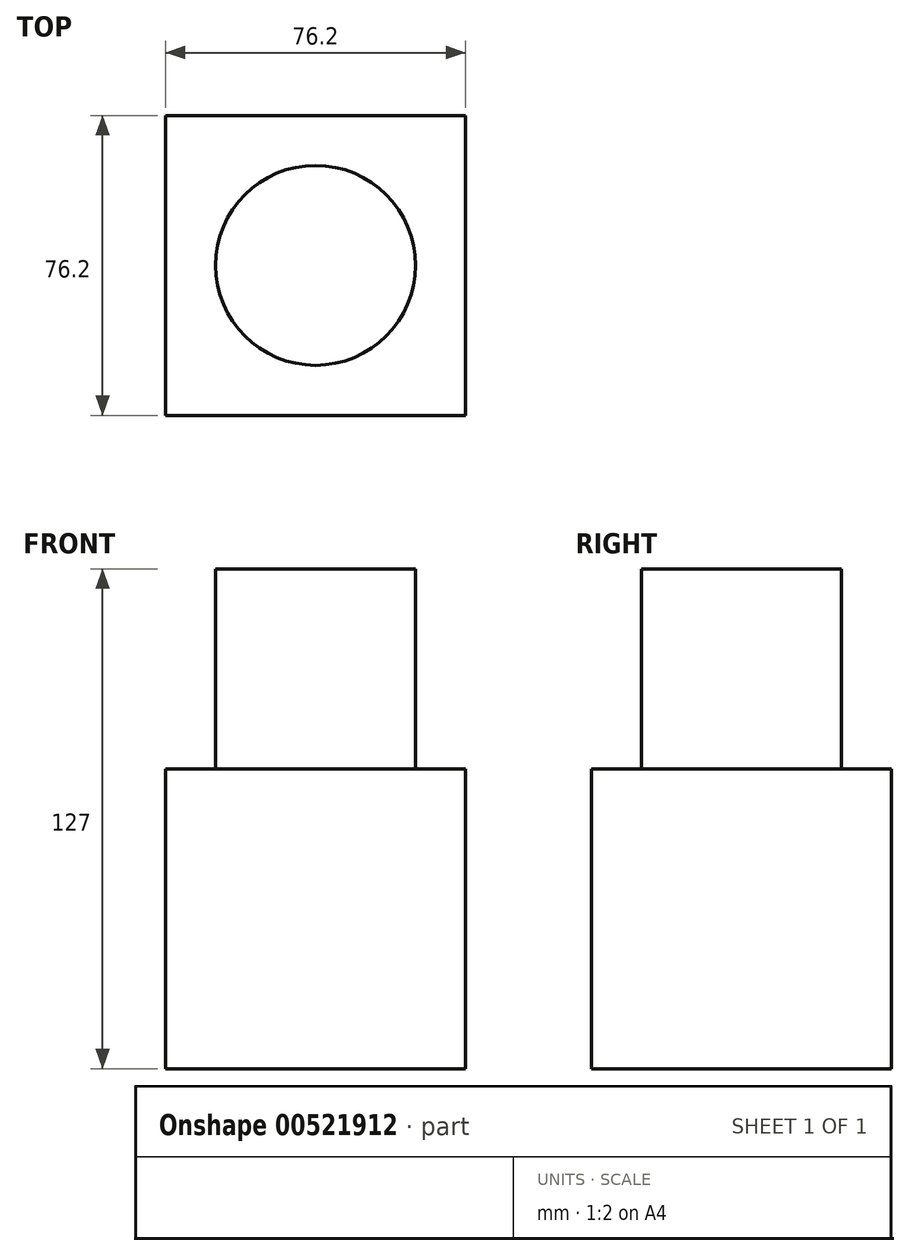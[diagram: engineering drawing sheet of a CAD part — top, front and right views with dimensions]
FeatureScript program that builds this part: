
annotation { "Feature Type Name" : "Feature", "Feature Type Description" : "" }
export const myFeature = defineFeature(function(context is Context, id is Id, definition is map)
    precondition{}
    {
        {
            var Q0;
            Q0=qCreatedBy(makeId("Top.planeOp"),FACE);
            var sketch = newSketch(context, id + "F0", { "sketchPlane" : qUnion([Q0])});
            skLineSegment(sketch, "E0.bottom", {"start": v(-38.1, -38.1) * mm, "end": v(38.1, -38.1) * mm});
            skLineSegment(sketch, "E0.top", {"start": v(-38.1, 38.1) * mm, "end": v(38.1, 38.1) * mm});
            skLineSegment(sketch, "E0.left", {"start": v(-38.1, -38.1) * mm, "end": v(-38.1, 38.1) * mm});
            skLineSegment(sketch, "E0.right", {"start": v(38.1, -38.1) * mm, "end": v(38.1, 38.1) * mm});
            skLineSegment(sketch, "E1", {"start": v(-38.1, 38.1) * mm, "end": v(38.1, -38.1) * mm, "construction": true});
            skSolve(sketch);
        }
        {
            var Q0;
            Q0 = qSketchRegion(id + "F0", true);
            extrude(context, id + "F1", {"entities" : qUnion([Q0]), "depth" : 76.2 * mm, "offsetDistance" : 25.4 * mm, "symmetric" : true});
        }
        {
            var Q0;
            Q0=makeQuery(id+"F1.opExtrude","CAP_FACE",FACE,{"disambiguationData":[OSD([sQuery(id+"F0.wireOp",EDGE,"E0.bottom"),sQuery(id+"F0.wireOp",EDGE,"E0.top"),sQuery(id+"F0.wireOp",EDGE,"E0.left"),sQuery(id+"F0.wireOp",EDGE,"E0.right")])],"isStart":false});
            var sketch = newSketch(context, id + "F2", { "sketchPlane" : qUnion([Q0])});
            skCircle(sketch, "E2", {"center": v(0, 0) * mm, "radius": 25.4 * mm});
            skSolve(sketch);
        }
        {
            var Q0;
            Q0 = qSketchRegion(id + "F2", true);
            extrude(context, id + "F3", {"entities" : qUnion([Q0]), "operationType" : NewBodyOperationType.ADD, "depth" : 50.8 * mm, "offsetDistance" : 25.4 * mm});
        }
    });
